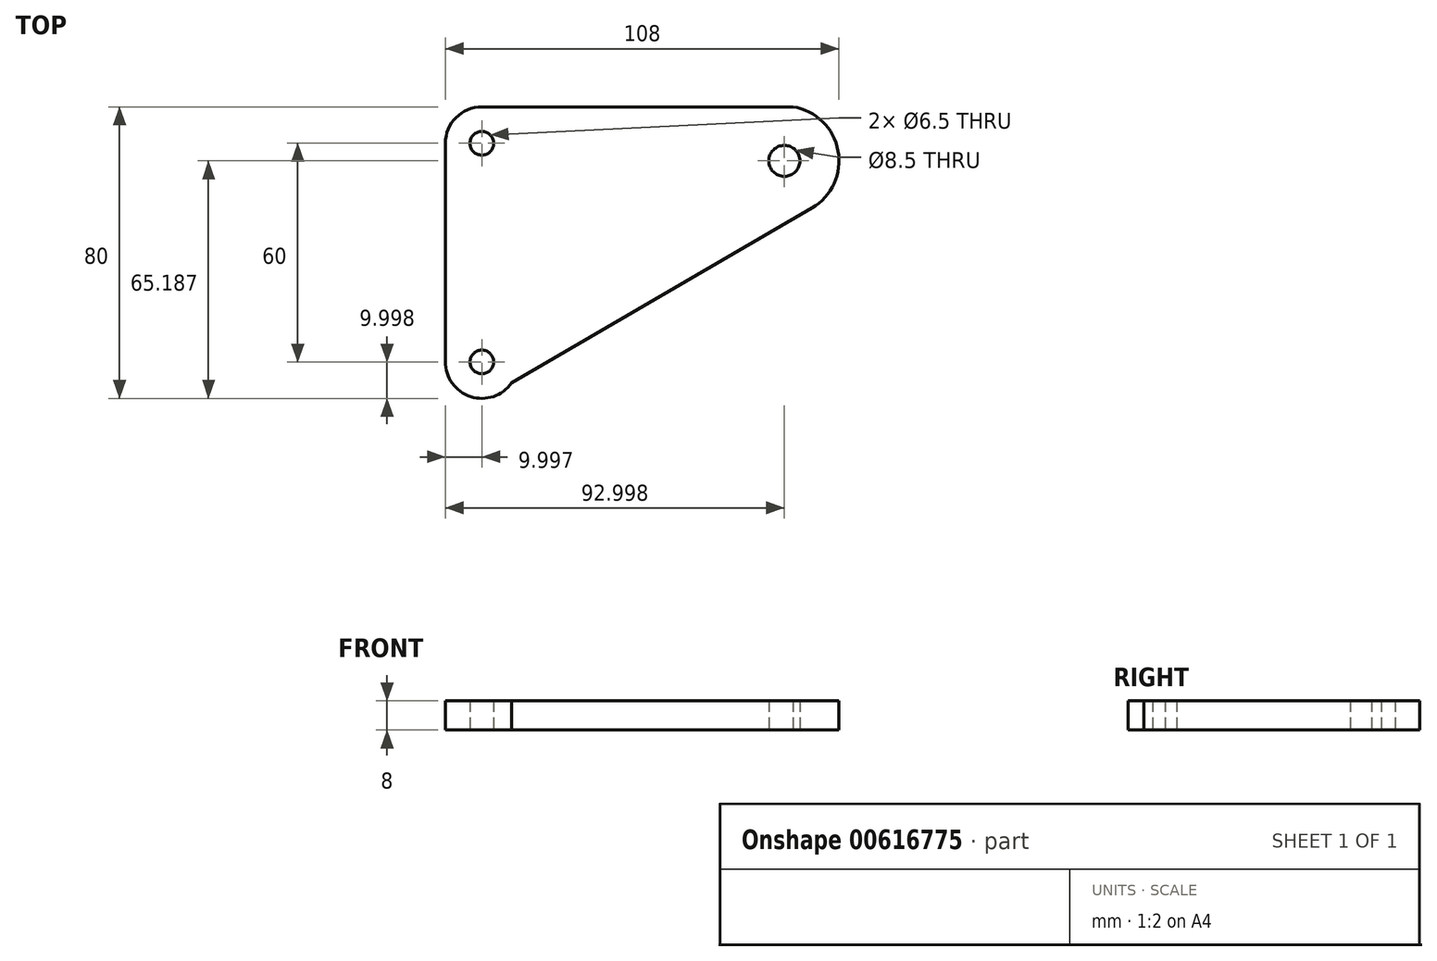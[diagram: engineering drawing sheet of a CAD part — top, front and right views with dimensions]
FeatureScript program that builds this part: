
annotation { "Feature Type Name" : "Feature", "Feature Type Description" : "" }
export const myFeature = defineFeature(function(context is Context, id is Id, definition is map)
    precondition{}
    {
        {
            var Q0;
            Q0=qCreatedBy(makeId("Top.planeOp"),FACE);
            var sketch = newSketch(context, id + "F0", { "sketchPlane" : qUnion([Q0])});
            skCircle(sketch, "E0", {"center": v(-62.86, 16.69) * mm, "radius": 3.25 * mm});
            skCircle(sketch, "E1", {"center": v(-62.86, -43.31) * mm, "radius": 3.25 * mm});
            skCircle(sketch, "E2", {"center": v(20.14, 11.88) * mm, "radius": 4.25 * mm});
            skArc(sketch, "E3", {"start": v(-62.86, 26.69) * mm, "mid": v(-69.93, 23.76) * mm, "end": v(-72.86, 16.69) * mm});
            skArc(sketch, "E4", {"start": v(-72.86, -43.2) * mm, "mid": v(-65.93, -52.83) * mm, "end": v(-54.68, -49.05) * mm});
            skArc(sketch, "E5", {"start": v(27.69, -1.08) * mm, "mid": v(34.26, 16.92) * mm, "end": v(17.76, 26.69) * mm});
            skLineSegment(sketch, "E6", {"start": v(-72.86, -43.2) * mm, "end": v(-72.86, 16.69) * mm});
            skLineSegment(sketch, "E7", {"start": v(-54.68, -49.05) * mm, "end": v(29.55, 0) * mm});
            skLineSegment(sketch, "E8", {"start": v(22.51, 26.69) * mm, "end": v(-62.86, 26.69) * mm});
            skSolve(sketch);
        }
        {
            var Q0;
            Q0=makeQuery(id+"F0.imprint","IMPRINT",FACE,{"disambiguationData":[TD([[makeQuery(id+"F0.imprint","IMPRINT",EDGE,{"derivedFrom":sQuery(id+"F0.wireOp",EDGE,"E0")}),-1.0]])]});
            extrude(context, id + "F1", {"entities" : qUnion([Q0]), "depth" : 8 * mm, "offsetDistance" : 25 * mm});
        }
    });
